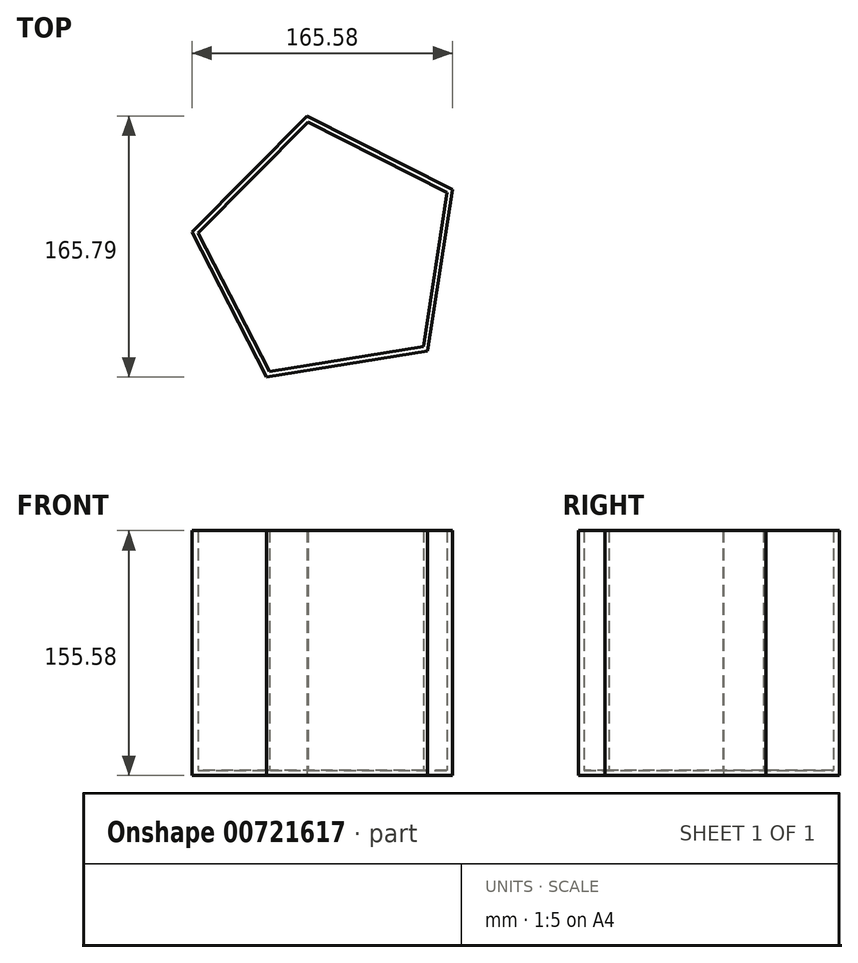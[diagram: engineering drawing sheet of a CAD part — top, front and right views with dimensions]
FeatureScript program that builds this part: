
annotation { "Feature Type Name" : "Feature", "Feature Type Description" : "" }
export const myFeature = defineFeature(function(context is Context, id is Id, definition is map)
    precondition{}
    {
        {
            var Q0;
            Q0=qCreatedBy(makeId("Top.planeOp"),FACE);
            var sketch = newSketch(context, id + "F0", { "sketchPlane" : qUnion([Q0])});
            skCircle(sketch, "E0.cCircle", {"center": v(0, 0) * mm, "radius": 68.17 * mm, "construction": true});
            skLineSegment(sketch, "E0.0", {"start": v(-13.51, 83.17) * mm, "end": v(74.93, 38.55) * mm});
            skLineSegment(sketch, "E0.1", {"start": v(74.93, 38.55) * mm, "end": v(59.82, -59.35) * mm});
            skLineSegment(sketch, "E0.2", {"start": v(59.82, -59.35) * mm, "end": v(-37.96, -75.23) * mm});
            skLineSegment(sketch, "E0.3", {"start": v(-37.96, -75.23) * mm, "end": v(-83.28, 12.85) * mm});
            skLineSegment(sketch, "E0.4", {"start": v(-83.28, 12.85) * mm, "end": v(-13.51, 83.17) * mm});
            skPoint(sketch, "E0.0.midPoint", {"position": v(30.7, 60.86) * mm});
            skSolve(sketch);
        }
        {
            var Q0;
            Q0 = qSketchRegion(id + "F0", true);
            extrude(context, id + "F1", {"entities" : qUnion([Q0]), "depth" : 152.4 * mm, "offsetDistance" : 25.4 * mm});
        }
        {
            var Q0;
            Q0=makeQuery(id+"F1.opExtrude","CAP_FACE",FACE,{"disambiguationData":[OSD([sQuery(id+"F0.wireOp",EDGE,"E0.0"),sQuery(id+"F0.wireOp",EDGE,"E0.1"),sQuery(id+"F0.wireOp",EDGE,"E0.2"),sQuery(id+"F0.wireOp",EDGE,"E0.3"),sQuery(id+"F0.wireOp",EDGE,"E0.4")])],"isStart":false});
            shell(context, id + "F2", {"entities" : qUnion([Q0]), "thickness" : 3.17 * mm, "oppositeDirection" : true});
        }
    });
